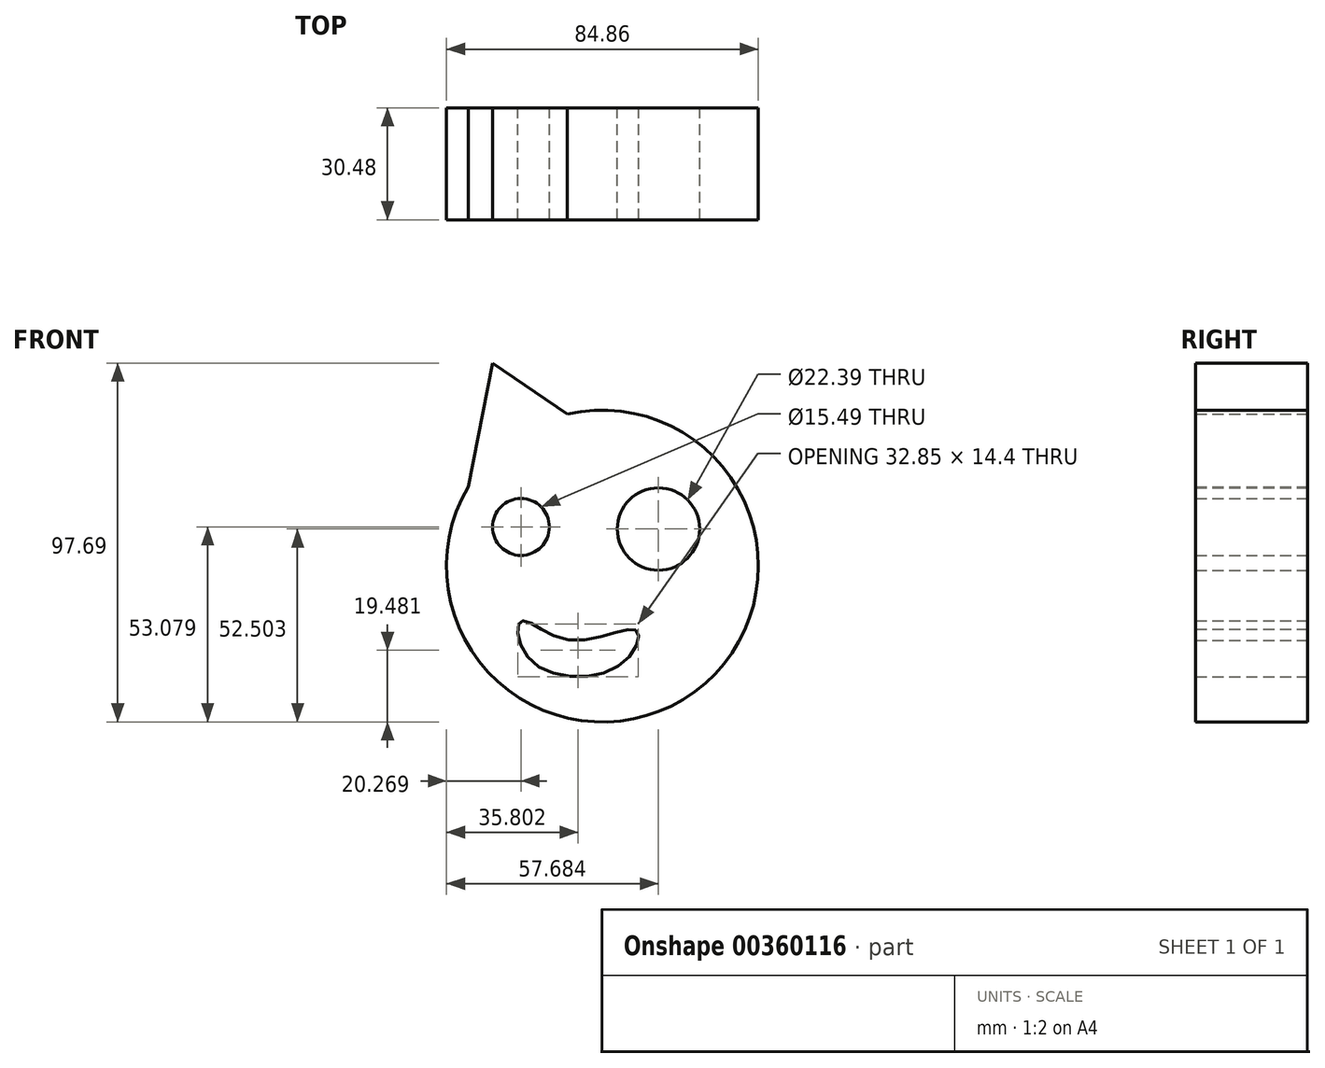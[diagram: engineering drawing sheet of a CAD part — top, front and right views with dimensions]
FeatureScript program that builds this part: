
annotation { "Feature Type Name" : "Feature", "Feature Type Description" : "" }
export const myFeature = defineFeature(function(context is Context, id is Id, definition is map)
    precondition{}
    {
        {
            var Q0;
            Q0=qCreatedBy(makeId("Front.planeOp"),FACE);
            var sketch = newSketch(context, id + "F0", { "sketchPlane" : qUnion([Q0])});
            skCircle(sketch, "E0", {"center": v(0, 0) * mm, "radius": 42.43 * mm});
            skPoint(sketch, "E1", {"position": v(-36.53, 21.57) * mm});
            skPoint(sketch, "E2", {"position": v(-29.93, 55.26) * mm});
            skPoint(sketch, "E3", {"position": v(-9.57, 41.33) * mm});
            skPoint(sketch, "E4", {"position": v(21.99, 36.28) * mm});
            skPoint(sketch, "E5", {"position": v(38.28, 51.23) * mm});
            skPoint(sketch, "E6", {"position": v(39.09, 16.5) * mm});
            skCircle(sketch, "E7", {"center": v(-22.16, 10.65) * mm, "radius": 7.74 * mm});
            skCircle(sketch, "E8", {"center": v(15.25, 10.07) * mm, "radius": 11.2 * mm});
            skPoint(sketch, "E9", {"position": v(-11.8, -3.17) * mm});
            skPoint(sketch, "E10", {"position": v(0, -4.9) * mm});
            skPoint(sketch, "E11", {"position": v(-7.48, -12.66) * mm});
            skLineSegment(sketch, "E12", {"start": v(-29.93, 55.26) * mm, "end": v(-36.53, 21.57) * mm});
            skLineSegment(sketch, "E13", {"start": v(-29.93, 55.26) * mm, "end": v(-9.57, 41.33) * mm});
            skLineSegment(sketch, "E14", {"start": v(21.99, 36.28) * mm, "end": v(31.66, 46.62) * mm});
            skLineSegment(sketch, "E15", {"start": v(31.66, 46.62) * mm, "end": v(38.28, 51.23) * mm});
            skLineSegment(sketch, "E16", {"start": v(39.09, 16.5) * mm, "end": v(39.09, 51.23) * mm});
            skLineSegment(sketch, "E17", {"start": v(-11.8, -3.17) * mm, "end": v(0, -4.9) * mm});
            skLineSegment(sketch, "E18", {"start": v(0, -4.9) * mm, "end": v(-7.48, -12.66) * mm});
            skLineSegment(sketch, "E19", {"start": v(-7.48, -12.66) * mm, "end": v(-11.8, -3.17) * mm});
            skPoint(sketch, "E20", {"position": v(-9.2, -20.15) * mm});
            skPoint(sketch, "E21", {"position": v(-22.16, -14.97) * mm});
            skPoint(sketch, "E22", {"position": v(9.2, -17.56) * mm});
            skFitSpline(sketch, "E23", {"points": [v(-22.16, -14.97) * mm, v(-9.2, -20.15) * mm, v(9.2, -17.56) * mm, v(4.6, -27.05) * mm, v(-19.57, -25.61) * mm, v(-22.16, -14.97) * mm]});
            skLineSegment(sketch, "E24", {"start": v(-9.2, -20.15) * mm, "end": v(-7.48, -12.66) * mm});
            skLineSegment(sketch, "E25", {"start": v(22.16, -7.48) * mm, "end": v(39.14, -3.74) * mm});
            skLineSegment(sketch, "E26", {"start": v(20.43, -16.4) * mm, "end": v(33.67, -19.57) * mm});
            skLineSegment(sketch, "E27", {"start": v(-27.05, -2.3) * mm, "end": v(-38.57, 3.17) * mm});
            skLineSegment(sketch, "E28", {"start": v(-41.51, -8.74) * mm, "end": v(-31.95, -8.74) * mm});
            skArc(sketch, "E29", {"start": v(-19.57, 28.2) * mm, "mid": v(-26.9, 28.4) * mm, "end": v(-30.22, 21.87) * mm});
            skArc(sketch, "E30", {"start": v(26.2, 21.87) * mm, "mid": v(25.93, 26.52) * mm, "end": v(21.59, 28.2) * mm});
            skSolve(sketch);
        }
        {
            var Q0;
            {var subQ0=sQuery(id+"F0.wireOp",EDGE,"E12");Q0=makeQuery(id+"F0.imprint","IMPRINT",FACE,{"disambiguationData":[TD([[makeQuery(id+"F0.imprint","IMPRINT",EDGE,{"derivedFrom":subQ0}),1.0]])]});}
            var Q1;
            Q1=makeQuery(id+"F0.imprint","IMPRINT",FACE,{"disambiguationData":[TD([[makeQuery(id+"F0.imprint","IMPRINT",EDGE,{"derivedFrom":sQuery(id+"F0.wireOp",EDGE,"E7")}),-1.0]])]});
            var Q2;
            Q2=makeQuery(id+"F0.imprint","IMPRINT",FACE,{"disambiguationData":[TD([[makeQuery(id+"F0.imprint","IMPRINT",EDGE,{"derivedFrom":sQuery(id+"F0.wireOp",EDGE,"E17")}),-1.0]])]});
            var Q3;
            Q3=sQuery(id+"F0.wireOp",EDGE,"E17");
            var Q4;
            Q4=sQuery(id+"F0.wireOp",EDGE,"E19");
            var Q5;
            Q5=sQuery(id+"F0.wireOp",EDGE,"E18");
            extrude(context, id + "F1", {"entities" : qUnion([Q0, Q1, Q2]), "surfaceEntities" : qUnion([Q3, Q4, Q5]), "depth" : 30.48 * mm});
        }
    });
